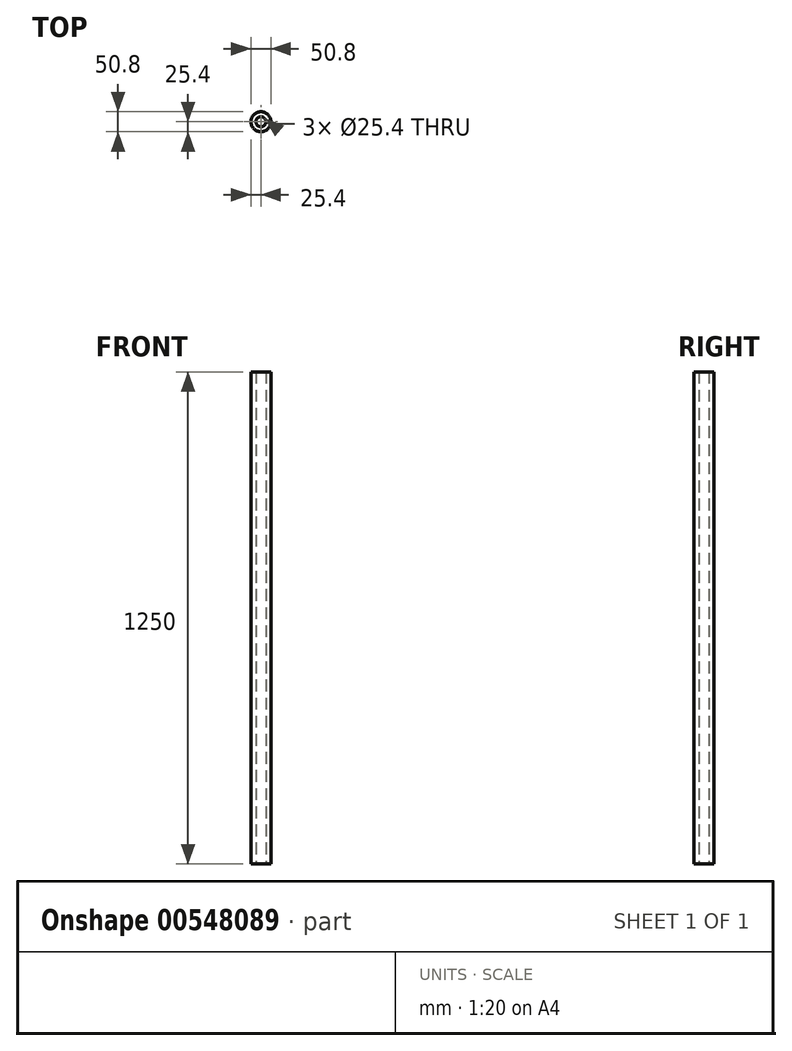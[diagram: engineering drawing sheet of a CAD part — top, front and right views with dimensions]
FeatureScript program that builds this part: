
annotation { "Feature Type Name" : "Feature", "Feature Type Description" : "" }
export const myFeature = defineFeature(function(context is Context, id is Id, definition is map)
    precondition{}
    {
        {
            var Q0;
            Q0=qCreatedBy(makeId("Top.planeOp"),FACE);
            var sketch = newSketch(context, id + "F0", { "sketchPlane" : qUnion([Q0])});
            skCircle(sketch, "E0", {"center": v(0, 0) * mm, "radius": 25.4 * mm});
            skCircle(sketch, "E1", {"center": v(0, 0) * mm, "radius": 12.7 * mm});
            skSolve(sketch);
        }
        {
            var Q0;
            Q0 = qSketchRegion(id + "F0", true);
            extrude(context, id + "F1", {"entities" : qUnion([Q0]), "depth" : 1250 * mm, "offsetDistance" : 25.4 * mm});
        }
    });
